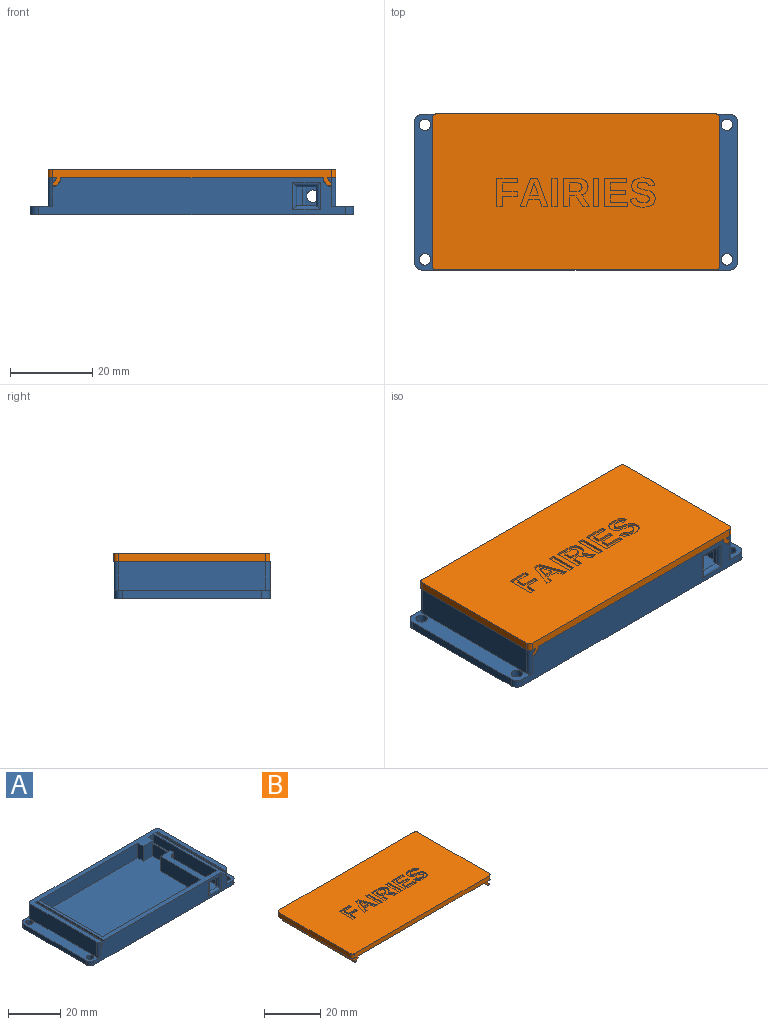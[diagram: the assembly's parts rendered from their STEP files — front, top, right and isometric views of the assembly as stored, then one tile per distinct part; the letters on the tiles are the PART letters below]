
ASSEMBLY  parts=2 mates=1
PART A: 64 faces, bbox 78.8x38x9 mm
  f0: plane 78.78x38mm, normal (0,0,-1), area 2965.4mm2, adj f9,f14,f54,f55,f56,f57,f58,f59
  f1: plane 38x5.39mm, normal (0,0,1), area 153.1mm2, adj f6,f7,f8,f9,f14,f54,f58,f59
  f2: plane 38x5.39mm, normal (0,0,1), area 153.1mm2, adj f3,f4,f5,f9,f14,f55,f56,f57
  f3: plane 36x7mm, normal (1,0,0), area 252mm2, adj f2,f4,f5,f12
  f4: cylinder r=1mm len=7mm, axis (0,0,1), area 11mm2, adj f2,f3,f9,f11,f12,f44
  f5: cylinder r=1mm len=7mm, axis (0,0,-1), area 11mm2, adj f2,f3,f12,f14
  f6: plane 36x7mm, normal (-1,0,0), area 252mm2, adj f1,f7,f8,f12
  f7: cylinder r=1mm len=7mm, axis (0,0,1), area 11mm2, adj f1,f6,f12,f14
  f8: cylinder r=1mm len=7mm, axis (0,0,-1), area 11mm2, adj f1,f6,f9,f10,f12,f52
  f9: plane 74.78x9mm, normal (0,-1,0), area 573.8mm2, adj f0,f1,f2,f4,f8,f12,f37,f38
  f10: plane 1.26x0.85mm, normal (0,-1,0), area 0.7mm2, adj f8,f12,f50,f51,f52
  f11: plane 1.26x0.85mm, normal (0,-1,0), area 0.7mm2, adj f4,f12,f44,f45,f46
  f12: plane 70x38mm, normal (0,0,1), area 542.9mm2, adj f3,f4,f5,f6,f7,f8,f9,f10
  f13: plane 4.5x3mm, normal (0,-1,0), area 10mm2, adj f12,f15,f17,f41
  f14: plane 74.78x9mm, normal (0,1,0), area 618.5mm2, adj f0,f1,f2,f5,f7,f12,f41,f60
  f15: plane 34.1x6.8mm, normal (-1,0,0), area 231.9mm2, adj f12,f13,f16,f21,f22
  f16: plane 3x2.3mm, normal (0,-1,0), area 3.4mm2, adj f15,f17,f22,f41
  f17: plane 13.24x6.8mm, normal (1,0,0), area 80.7mm2, adj f12,f13,f16,f22,f23,f29,f32,f33
  f18: plane 6.8x0.17mm, normal (0.02,-1,0), area 1.2mm2, adj f12,f19,f22,f33
  f19: cylinder r=2mm len=6.8mm, axis (0,0,1), area 21mm2, adj f12,f18,f20,f22
  f20: plane 17.86x6.8mm, normal (1,0,0), area 121.5mm2, adj f12,f19,f21,f22
  f21: plane 6.8x6.1mm, normal (0,1,0), area 19.4mm2, adj f12,f15,f20,f22,f34,f35,f36
  f22: plane 35.05x6.1mm, normal (0,0,1), area 167.8mm2, adj f15,f16,f17,f18,f19,f20,f21,f33
  f23: plane 6.8x5.67mm, normal (0,-1,0), area 33.6mm2, adj f12,f17,f24,f30,f31,f32
  f24: plane 6.8x3mm, normal (-1,0,0), area 20.4mm2, adj f12,f23,f25,f31
  f25: plane 53.2x6.8mm, normal (0,-1,0), area 361.8mm2, adj f12,f24,f26,f31
  f26: plane 34.1x6.8mm, normal (1,0,0), area 231.9mm2, adj f12,f25,f27,f31
  f27: plane 53.2x6.8mm, normal (0,1,0), area 361.8mm2, adj f12,f26,f28,f31
  f28: plane 21.84x6.8mm, normal (-1,0,0), area 148.5mm2, adj f12,f27,f29,f31
  f29: plane 6.8x5.67mm, normal (0,1,0), area 33.6mm2, adj f12,f17,f28,f30,f31,f32
  f30: plane 9.26x5.8mm, normal (-1,0,0), area 53.7mm2, adj f23,f29,f31,f32
  f31: plane 58.02x34.1mm, normal (0,0,1), area 1858.8mm2, adj f23,f24,f25,f26,f27,f28,f29,f30
  f32: plane 9.26x0.85mm, normal (0,0,1), area 7.8mm2, adj f17,f23,f29,f30
  f33: cylinder r=1mm len=6.8mm, axis (0,0,1), area 10.5mm2, adj f12,f17,f18,f22
  f34: plane 4.6x0.95mm, normal (-1,0,0), area 4.4mm2, adj f21,f22,f35,f38
  f35: plane 4.8x0.95mm, normal (0,0,-1), area 4.6mm2, adj f21,f34,f36,f40
  f36: plane 4.6x0.95mm, normal (1,0,0), area 4.4mm2, adj f21,f22,f35,f39
  f37: cylinder r=1mm len=6.8mm, axis (-1,0,0), area 8.7mm2, adj f9,f22,f38,f39
  f38: cylinder r=1mm len=6.6mm, axis (0,0,-1), area 8.4mm2, adj f9,f34,f37,f40
  f39: cylinder r=1mm len=6.6mm, axis (0,0,1), area 8.4mm2, adj f9,f36,f37,f40
  f40: cylinder r=1mm len=6.8mm, axis (1,0,0), area 8.7mm2, adj f9,f35,f38,f39
  f41: cylinder r=1.5mm len=3mm, axis (0,1,0), area 18.4mm2, adj f13,f14,f16
  f42: plane 36x0.85mm, normal (1,0,0), area 30.5mm2, adj f9,f12,f43,f47
  f43: plane 36x1.08mm, normal (0.71,0,0.71), area 54.8mm2, adj f9,f42,f44,f47
  f44: cylinder r=0.6mm len=36mm, axis (0,-1,0), area 67.9mm2, adj f4,f9,f11,f43,f45,f47
  f45: plane 36x0.72mm, normal (-0.71,0,-0.71), area 36.9mm2, adj f11,f44,f46,f47
  f46: plane 36x0.35mm, normal (-1,0,0), area 12.7mm2, adj f11,f12,f45,f47
  f47: plane 2.1x2.1mm, normal (0,-1,0), area 2.8mm2, adj f12,f42,f43,f44,f45,f46
  f48: plane 36x1.08mm, normal (-0.71,0,0.71), area 54.8mm2, adj f9,f49,f52,f53
  f49: plane 36x0.85mm, normal (-1,0,0), area 30.5mm2, adj f9,f12,f48,f53
  f50: plane 36x0.35mm, normal (1,0,0), area 12.7mm2, adj f10,f12,f51,f53
  f51: plane 36x0.72mm, normal (0.71,0,-0.71), area 36.9mm2, adj f10,f50,f52,f53
  f52: cylinder r=0.6mm len=36mm, axis (0,-1,0), area 67.9mm2, adj f8,f9,f10,f48,f51,f53
  f53: plane 2.1x2.1mm, normal (0,-1,0), area 2.8mm2, adj f12,f48,f49,f50,f51,f52
  f54: plane 34x2mm, normal (-1,0,0), area 68mm2, adj f0,f1,f62,f63
  f55: plane 34x2mm, normal (1,0,0), area 68mm2, adj f0,f2,f60,f61
  f56: cylinder r=1.4mm len=2.8mm, axis (0,0,-1), area 17.6mm2, adj f0,f2
  f57: cylinder r=1.4mm len=2.8mm, axis (0,0,-1), area 17.6mm2, adj f0,f2
  f58: cylinder r=1.4mm len=2.8mm, axis (0,0,-1), area 17.6mm2, adj f0,f1
  f59: cylinder r=1.4mm len=2.8mm, axis (0,0,-1), area 17.6mm2, adj f0,f1
  f60: cylinder r=2mm len=2mm, axis (0,0,-1), area 6.3mm2, adj f0,f2,f14,f55
  f61: cylinder r=2mm len=2mm, axis (0,0,1), area 6.3mm2, adj f0,f2,f9,f55
  f62: cylinder r=2mm len=2mm, axis (0,0,1), area 6.3mm2, adj f0,f1,f14,f54
  f63: cylinder r=2mm len=2mm, axis (0,0,-1), area 6.3mm2, adj f0,f1,f9,f54
PART B: 125 faces, bbox 70x38x4 mm
  f0: plane 70x38mm, normal (0,0,1), area 2520.3mm2, adj f2,f3,f4,f5,f18,f19,f20,f21
  f1: plane 70x38mm, normal (0,0,-1), area 2587.1mm2, adj f2,f3,f4,f5,f6,f7,f11,f12
  f2: plane 68x4mm, normal (0,-1,0), area 140.6mm2, adj f0,f1,f6,f7,f8,f9,f10,f12
  f3: plane 36x2mm, normal (1,0,0), area 72mm2, adj f0,f1,f18,f19
  f4: plane 68x2mm, normal (0,1,0), area 136mm2, adj f0,f1,f19,f20
  f5: plane 36x2mm, normal (-1,0,0), area 72mm2, adj f0,f1,f20,f21
  f6: plane 36x0.71mm, normal (1,0,0), area 25.5mm2, adj f1,f2,f10,f11
  f7: plane 36x0.29mm, normal (-1,0,0), area 10.5mm2, adj f1,f2,f8,f11
  f8: plane 36x0.85mm, normal (-0.71,0,0.71), area 43.5mm2, adj f2,f7,f9,f11
  f9: cylinder r=0.5mm len=36mm, axis (0,-1,0), area 56.5mm2, adj f2,f8,f10,f11
  f10: plane 36x1.15mm, normal (0.71,0,-0.71), area 58.4mm2, adj f2,f6,f9,f11
  f11: plane 2x2mm, normal (0,1,0), area 2.3mm2, adj f1,f6,f7,f8,f9,f10
  f12: plane 36x0.29mm, normal (1,0,0), area 10.5mm2, adj f1,f2,f16,f17
  f13: plane 36x0.71mm, normal (-1,0,0), area 25.5mm2, adj f1,f2,f14,f17
  f14: plane 36x1.15mm, normal (-0.71,0,-0.71), area 58.4mm2, adj f2,f13,f15,f17
  f15: cylinder r=0.5mm len=36mm, axis (0,-1,0), area 56.5mm2, adj f2,f14,f16,f17
  f16: plane 36x0.85mm, normal (0.71,0,0.71), area 43.5mm2, adj f2,f12,f15,f17
  f17: plane 2x2mm, normal (0,1,0), area 2.3mm2, adj f1,f12,f13,f14,f15,f16
  f18: cylinder r=1mm len=2mm, axis (0,0,1), area 3.1mm2, adj f0,f1,f2,f3
  f19: cylinder r=1mm len=2mm, axis (0,0,-1), area 3.1mm2, adj f0,f1,f3,f4
  f20: cylinder r=1mm len=2mm, axis (0,0,1), area 3.1mm2, adj f0,f1,f4,f5
  f21: cylinder r=1mm len=2mm, axis (0,0,-1), area 3.1mm2, adj f0,f1,f2,f5
  f22: plane 6.92x0.5mm, normal (1,0,0), area 3.5mm2, adj f0,f23,f25,f26
  f23: plane 1.45x0.5mm, normal (0,1,0), area 0.7mm2, adj f0,f22,f24,f26
  f24: plane 6.92x0.5mm, normal (-1,0,0), area 3.5mm2, adj f0,f23,f25,f26
  f25: plane 1.45x0.5mm, normal (0,-1,0), area 0.7mm2, adj f0,f22,f24,f26
  f26: plane 6.92x1.45mm, normal (0,0,1), area 10mm2, adj f22,f23,f24,f25
  f27: plane 6.92x0.5mm, normal (1,0,0), area 3.5mm2, adj f0,f28,f30,f31
  f28: plane 1.45x0.5mm, normal (0,1,0), area 0.7mm2, adj f0,f27,f29,f31
  f29: plane 6.92x0.5mm, normal (-1,0,0), area 3.5mm2, adj f0,f28,f30,f31
  f30: plane 1.45x0.5mm, normal (0,-1,0), area 0.7mm2, adj f0,f27,f29,f31
  f31: plane 6.92x1.45mm, normal (0,0,1), area 10mm2, adj f27,f28,f29,f30
  f32: plane 6.92x0.5mm, normal (1,0,0), area 3.5mm2, adj f0,f33,f43,f44
  f33: plane 5.65x0.5mm, normal (0,1,0), area 2.8mm2, adj f0,f32,f34,f44
  f34: plane 1.12x0.5mm, normal (-1,0,0), area 0.6mm2, adj f0,f33,f35,f44
  f35: plane 4.2x0.5mm, normal (0,-1,0), area 2.1mm2, adj f0,f34,f36,f44
  f36: plane 1.82x0.5mm, normal (-1,0,0), area 0.9mm2, adj f0,f35,f37,f44
  f37: plane 3.7x0.5mm, normal (0,1,0), area 1.8mm2, adj f0,f36,f38,f44
  f38: plane 1.12x0.5mm, normal (-1,0,0), area 0.6mm2, adj f0,f37,f39,f44
  f39: plane 3.7x0.5mm, normal (0,-1,0), area 1.8mm2, adj f0,f38,f40,f44
  f40: plane 1.74x0.5mm, normal (-1,0,0), area 0.9mm2, adj f0,f39,f41,f44
  f41: plane 4x0.5mm, normal (0,1,0), area 2mm2, adj f0,f40,f42,f44
  f42: plane 1.12x0.5mm, normal (-1,0,0), area 0.6mm2, adj f0,f41,f43,f44
  f43: plane 5.44x0.5mm, normal (0,-1,0), area 2.7mm2, adj f0,f32,f42,f44
  f44: plane 6.92x5.65mm, normal (0,0,1), area 23.3mm2, adj f32,f33,f34,f35,f36,f37,f38,f39
  f45: extruded ~1.56x0.75mm, area 0.9mm2, adj f0,f46,f75,f76
  f46: extruded ~0.76x0.5mm, area 0.4mm2, adj f0,f45,f47,f76
  f47: extruded ~0.57x0.5mm, area 0.3mm2, adj f0,f46,f48,f76
  f48: extruded ~0.68x0.5mm, area 0.4mm2, adj f0,f47,f49,f76
  f49: extruded ~1.43x0.5mm, area 0.7mm2, adj f0,f48,f50,f76
  f50: extruded ~1.11x0.5mm, area 0.6mm2, adj f0,f49,f51,f76
  f51: extruded ~0.5x0.42mm, area 0.3mm2, adj f0,f50,f52,f76
  f52: extruded ~0.5x0.44mm, area 0.2mm2, adj f0,f51,f53,f76
  f53: extruded ~1.32x0.83mm, area 0.9mm2, adj f0,f52,f54,f76
  f54: extruded ~0.95x0.5mm, area 0.5mm2, adj f0,f53,f55,f76
  f55: extruded ~0.67x0.5mm, area 0.4mm2, adj f0,f54,f56,f76
  f56: plane 1.41x0.5mm, normal (-0.14,0.99,0), area 0.7mm2, adj f0,f55,f57,f76
  f57: extruded ~1.33x0.83mm, area 0.8mm2, adj f0,f56,f58,f76
  f58: extruded ~1.93x0.5mm, area 1mm2, adj f0,f57,f59,f76
  f59: extruded ~2.05x0.5mm, area 1.1mm2, adj f0,f58,f60,f76
  f60: extruded ~1.44x0.71mm, area 0.8mm2, adj f0,f59,f61,f76
  f61: extruded ~0.65x0.5mm, area 0.3mm2, adj f0,f60,f62,f76
  f62: extruded ~0.5x0.5mm, area 0.3mm2, adj f0,f61,f63,f76
  f63: extruded ~0.5x0.42mm, area 0.3mm2, adj f0,f62,f64,f76
  f64: extruded ~0.55x0.5mm, area 0.3mm2, adj f0,f63,f65,f76
  f65: extruded ~1.08x0.5mm, area 0.6mm2, adj f0,f64,f66,f76
  f66: extruded ~1.22x0.5mm, area 0.6mm2, adj f0,f65,f67,f76
  f67: extruded ~0.5x0.49mm, area 0.3mm2, adj f0,f66,f68,f76
  f68: extruded ~0.5x0.49mm, area 0.3mm2, adj f0,f67,f69,f76
  f69: extruded ~1.52x0.92mm, area 1mm2, adj f0,f68,f70,f76
  f70: extruded ~1.14x0.5mm, area 0.6mm2, adj f0,f69,f71,f76
  f71: extruded ~0.8x0.56mm, area 0.5mm2, adj f0,f70,f72,f76
  f72: plane 1.4x0.5mm, normal (0.16,-0.99,0), area 0.7mm2, adj f0,f71,f73,f76
  f73: extruded ~1.43x0.97mm, area 0.9mm2, adj f0,f72,f74,f76
  f74: extruded ~2.09x0.5mm, area 1.1mm2, adj f0,f73,f75,f76
  f75: extruded ~2.21x0.54mm, area 1.2mm2, adj f0,f45,f74,f76
  f76: plane 7.13x6.03mm, normal (0,0,1), area 22mm2, adj f45,f46,f47,f48,f49,f50,f51,f52
  f77: plane 0.5x0.11mm, normal (-0.97,0.25,0), area 0.1mm2, adj f78,f91,f92,f123
  f78: plane 0.5x0.34mm, normal (0.96,0.29,0), area 0.2mm2, adj f77,f79,f92,f123
  f79: plane 0.67x0.5mm, normal (0.95,0.3,0), area 0.4mm2, adj f78,f80,f92,f123
  f80: plane 1.99x0.68mm, normal (0.95,0.33,0), area 1.1mm2, adj f79,f81,f92,f123
  f81: plane 1.99x0.5mm, normal (0,-1,0), area 1mm2, adj f80,f82,f92,f123
  f82: extruded ~2.49x0.85mm, area 1.3mm2, adj f81,f91,f92,f123
  f83: plane 1.77x0.61mm, normal (0.94,0.33,0), area 0.9mm2, adj f0,f84,f90,f92
  f84: plane 1.43x0.5mm, normal (0,1,0), area 0.7mm2, adj f0,f83,f85,f92
  f85: plane 6.92x2.52mm, normal (-0.94,-0.34,0), area 3.7mm2, adj f0,f84,f86,f92
  f86: plane 1.71x0.5mm, normal (0,-1,0), area 0.9mm2, adj f0,f85,f87,f92
  f87: plane 6.92x2.53mm, normal (0.94,-0.34,0), area 3.7mm2, adj f0,f86,f88,f92
  f88: plane 1.45x0.5mm, normal (0,1,0), area 0.7mm2, adj f0,f87,f89,f92
  f89: plane 1.77x0.61mm, normal (-0.94,0.33,0), area 0.9mm2, adj f0,f88,f90,f92
  f90: plane 2.64x0.5mm, normal (0,1,0), area 1.3mm2, adj f0,f83,f89,f92
  f91: extruded ~0.5x0.4mm, area 0.2mm2, adj f77,f82,f92,f123
  f92: plane 6.92x6.75mm, normal (0,0,1), area 20.6mm2, adj f77,f78,f79,f80,f81,f82,f83,f84
  f93: extruded ~1.28x1mm, area 0.9mm2, adj f94,f110,f111,f124
  f94: extruded ~0.77x0.5mm, area 0.4mm2, adj f93,f95,f111,f124
  f95: extruded ~0.92x0.5mm, area 0.5mm2, adj f94,f96,f111,f124
  f96: plane 1.9x0.5mm, normal (0,-1,0), area 0.9mm2, adj f95,f97,f111,f124
  f97: plane 2.04x0.5mm, normal (-1,0,0), area 1mm2, adj f96,f110,f111,f124
  f98: plane 2.63x1.61mm, normal (0.85,0.52,0), area 1.5mm2, adj f0,f99,f109,f111
  f99: plane 1.63x0.5mm, normal (0,1,0), area 0.8mm2, adj f0,f98,f100,f111
  f100: plane 2.91x1.87mm, normal (-0.84,-0.54,0), area 1.7mm2, adj f0,f99,f101,f111
  f101: extruded ~1.12x0.7mm, area 0.7mm2, adj f0,f100,f102,f111
  f102: extruded ~1.26x0.5mm, area 0.7mm2, adj f0,f101,f103,f111
  f103: extruded ~1.53x0.67mm, area 0.9mm2, adj f0,f102,f104,f111
  f104: extruded ~1.91x0.53mm, area 1mm2, adj f0,f103,f105,f111
  f105: plane 3.46x0.5mm, normal (0,-1,0), area 1.7mm2, adj f0,f104,f106,f111
  f106: plane 6.92x0.5mm, normal (1,0,0), area 3.5mm2, adj f0,f105,f107,f111
  f107: plane 1.45x0.5mm, normal (0,1,0), area 0.7mm2, adj f0,f106,f108,f111
  f108: plane 2.63x0.5mm, normal (-1,0,0), area 1.3mm2, adj f0,f107,f109,f111
  f109: plane 1.7x0.5mm, normal (0,1,0), area 0.8mm2, adj f0,f98,f108,f111
  f110: plane 1.86x0.5mm, normal (0,1,0), area 0.9mm2, adj f93,f97,f111,f124
  f111: plane 6.92x6.39mm, normal (0,0,1), area 25.9mm2, adj f93,f94,f95,f96,f97,f98,f99,f100
  f112: plane 2.14x0.5mm, normal (-1,0,0), area 1.1mm2, adj f0,f113,f121,f122
  f113: plane 3.66x0.5mm, normal (0,1,0), area 1.8mm2, adj f0,f112,f114,f122
  f114: plane 1.12x0.5mm, normal (-1,0,0), area 0.6mm2, adj f0,f113,f115,f122
  f115: plane 5.11x0.5mm, normal (0,-1,0), area 2.6mm2, adj f0,f114,f116,f122
  f116: plane 6.92x0.5mm, normal (1,0,0), area 3.5mm2, adj f0,f115,f117,f122
  f117: plane 1.45x0.5mm, normal (0,1,0), area 0.7mm2, adj f0,f116,f118,f122
  f118: plane 2.54x0.5mm, normal (-1,0,0), area 1.3mm2, adj f0,f117,f119,f122
  f119: plane 3.54x0.5mm, normal (0,1,0), area 1.8mm2, adj f0,f118,f120,f122
  f120: plane 1.12x0.5mm, normal (-1,0,0), area 0.6mm2, adj f0,f119,f121,f122
  f121: plane 3.54x0.5mm, normal (0,-1,0), area 1.8mm2, adj f0,f112,f120,f122
  f122: plane 6.92x5.11mm, normal (0,0,1), area 18.1mm2, adj f112,f113,f114,f115,f116,f117,f118,f119
  f123: plane 3x1.99mm, normal (0,0,1), area 2.9mm2, adj f77,f78,f79,f80,f81,f82,f91
  f124: plane 3.14x2.04mm, normal (0,0,1), area 6mm2, adj f93,f94,f95,f96,f97,f110
PLACE A t=(30.63,21.96,-52.92)mm
PLACE B t=(30.63,21.99,-43.92)mm
MATE slider A.f44 <-> B.f15  axis (0,-1,0) through (64.08,2.96,-45.42)mm
